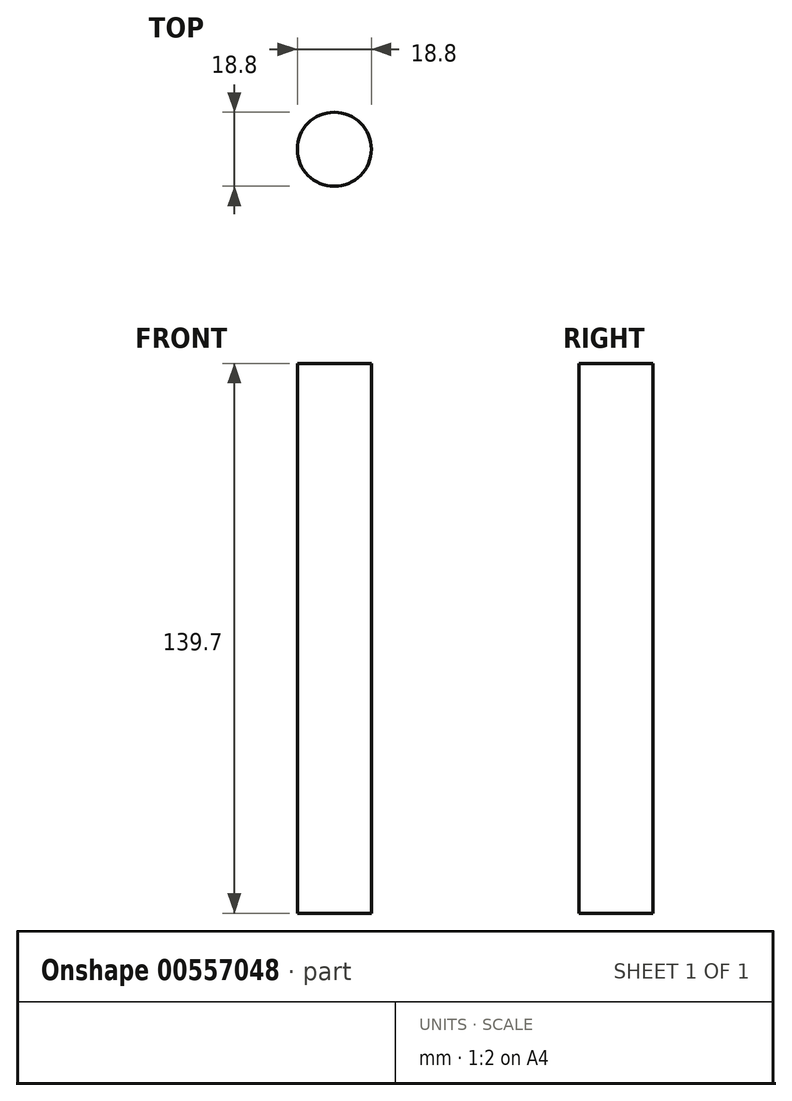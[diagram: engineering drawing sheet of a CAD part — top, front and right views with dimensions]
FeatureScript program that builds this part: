
annotation { "Feature Type Name" : "Feature", "Feature Type Description" : "" }
export const myFeature = defineFeature(function(context is Context, id is Id, definition is map)
    precondition{}
    {
        {
            var Q0;
            Q0=qCreatedBy(makeId("Top.planeOp"),FACE);
            var sketch = newSketch(context, id + "F0", { "sketchPlane" : qUnion([Q0])});
            skCircle(sketch, "E0", {"center": v(0, 0) * mm, "radius": 9.4 * mm});
            skSolve(sketch);
        }
        {
            var Q0;
            Q0=sQuery(id+"F0.wireOp",EDGE,"E0");
            extrude(context, id + "F1", {"bodyType" : ToolBodyType.SURFACE, "surfaceEntities" : qUnion([Q0]), "depth" : 139.7 * mm, "offsetDistance" : 25.4 * mm});
        }
    });
